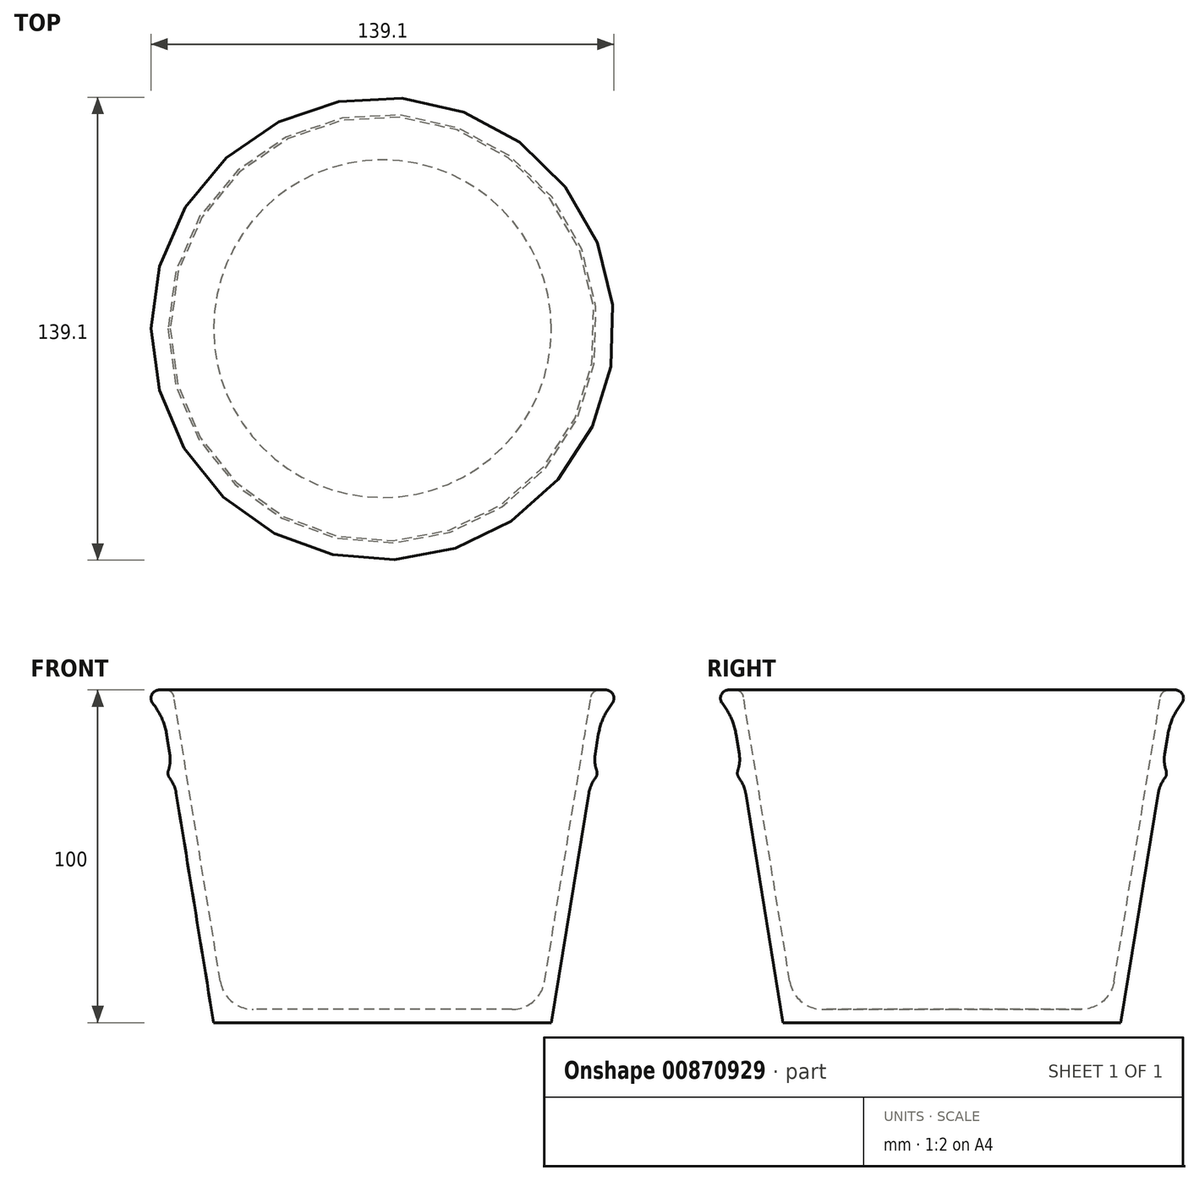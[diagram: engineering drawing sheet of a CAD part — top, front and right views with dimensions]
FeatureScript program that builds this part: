
annotation { "Feature Type Name" : "Feature", "Feature Type Description" : "" }
export const myFeature = defineFeature(function(context is Context, id is Id, definition is map)
    precondition{}
    {
        {
            var Q0;
            Q0=qCreatedBy(makeId("Front.planeOp"),FACE);
            var sketch = newSketch(context, id + "F0", { "sketchPlane" : qUnion([Q0])});
            skLineSegment(sketch, "E0", {"start": v(0, 5) * mm, "end": v(0, 97) * mm});
            skLineSegment(sketch, "E1", {"start": v(0, 97) * mm, "end": v(60, 97) * mm, "construction": true});
            skLineSegment(sketch, "E2", {"start": v(60, 97) * mm, "end": v(45, 5) * mm, "construction": true});
            skLineSegment(sketch, "E3", {"start": v(45, 5) * mm, "end": v(0, 5) * mm, "construction": true});
            skLineSegment(sketch, "E4", {"start": v(63, 100) * mm, "end": v(47.35, 4) * mm});
            skLineSegment(sketch, "E5", {"start": v(47.35, 4) * mm, "end": v(0, 4) * mm});
            skLineSegment(sketch, "E6", {"start": v(63, 100) * mm, "end": v(67.05, 100) * mm});
            skLineSegment(sketch, "E7", {"start": v(64.88, 86.66) * mm, "end": v(63.9, 80.7) * mm});
            skLineSegment(sketch, "E8", {"start": v(50.75, 0) * mm, "end": v(0, 0) * mm});
            skLineSegment(sketch, "E9", {"start": v(0, 0) * mm, "end": v(0, 4) * mm});
            skArc(sketch, "E10", {"start": v(69, 95.94) * mm, "mid": v(69.3, 98.58) * mm, "end": v(67.05, 100) * mm});
            skPoint(sketch, "E11.visualSharp", {"position": v(66.26, 95.13) * mm});
            skArc(sketch, "E11.filletArc", {"start": v(69, 95.94) * mm, "mid": v(66.34, 91.56) * mm, "end": v(64.88, 86.66) * mm});
            skArc(sketch, "E12", {"start": v(63.94, 73.47) * mm, "mid": v(64.43, 74.6) * mm, "end": v(64.33, 75.82) * mm});
            skLineSegment(sketch, "E13.trimOffspring", {"start": v(62, 68.98) * mm, "end": v(50.75, 0) * mm});
            skPoint(sketch, "E14.visualSharp", {"position": v(63.32, 77.1) * mm});
            skArc(sketch, "E14.filletArc", {"start": v(63.9, 80.7) * mm, "mid": v(63.81, 78.23) * mm, "end": v(64.33, 75.82) * mm});
            skPoint(sketch, "E15.visualSharp", {"position": v(62.58, 72.58) * mm});
            skArc(sketch, "E15.filletArc", {"start": v(63.94, 73.47) * mm, "mid": v(62.69, 71.35) * mm, "end": v(62, 68.98) * mm});
            skSolve(sketch);
        }
        {
            var Q0;
            Q0=makeQuery(id+"F0.imprint","IMPRINT",FACE,{"disambiguationData":[TD([[makeQuery(id+"F0.imprint","IMPRINT",EDGE,{"derivedFrom":sQuery(id+"F0.wireOp",EDGE,"E4")}),1.0]])]});
            var Q1;
            Q1=sQuery(id+"F0.wireOp",EDGE,"E0");
            revolve(context, id + "F1", {"surfaceOperationType" : NewSurfaceOperationType.NEW, "entities" : qUnion([Q0]), "axis" : qUnion([Q1]), "revolveType" : RevolveType.FULL});
        }
        {
            var Q0;
            Q0=makeQuery(id+"F1.opRevolve","SWEPT_EDGE",EDGE,{"disambiguationData":[OSD([sQuery(id+"F0.wireOp",EDGE,"E4"),sQuery(id+"F0.wireOp",EDGE,"E5")])]});
            fillet(context, id + "F2", {"entities" : qUnion([Q0]), "radius" : 10 * mm, "tangentPropagation" : true, "allowEdgeOverflow" : false});
        }
        {
            var Q0;
            Q0=makeQuery(id+"F1.opRevolve","SWEPT_EDGE",EDGE,{"disambiguationData":[OSD([sQuery(id+"F0.wireOp",EDGE,"E4"),sQuery(id+"F0.wireOp",EDGE,"E6")])]});
            fillet(context, id + "F3", {"entities" : qUnion([Q0]), "radius" : 2.5 * mm, "tangentPropagation" : true, "allowEdgeOverflow" : false});
        }
    });
